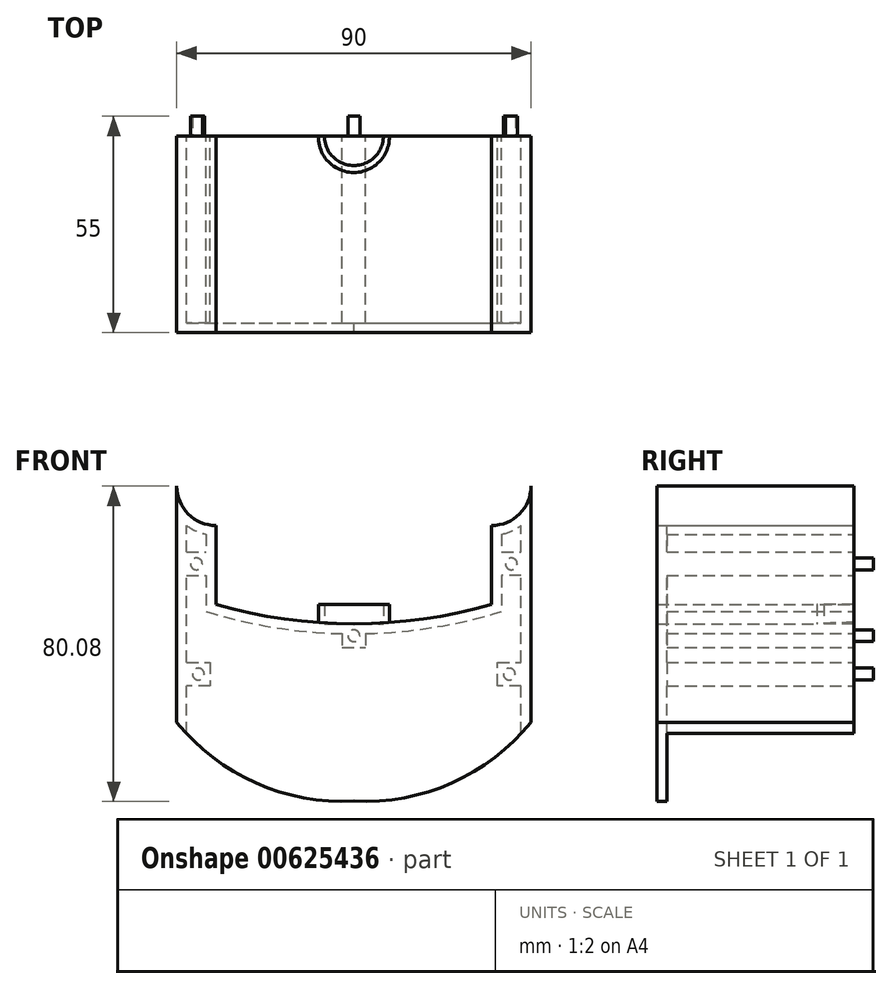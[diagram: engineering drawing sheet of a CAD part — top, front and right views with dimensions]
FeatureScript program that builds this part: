
annotation { "Feature Type Name" : "Feature", "Feature Type Description" : "" }
export const myFeature = defineFeature(function(context is Context, id is Id, definition is map)
    precondition{}
    {
        {
            var Q0;
            Q0=qCreatedBy(makeId("Front.planeOp"),FACE);
            var sketch = newSketch(context, id + "F0", { "sketchPlane" : qUnion([Q0])});
            skLineSegment(sketch, "E0.top", {"start": v(45, -25) * mm, "end": v(-45, -25) * mm});
            skLineSegment(sketch, "E0.left", {"start": v(45, 25) * mm, "end": v(45, -25) * mm});
            skLineSegment(sketch, "E0.right", {"start": v(-45, 25) * mm, "end": v(-45, -25) * mm});
            skPoint(sketch, "E0.middle", {"position": v(0, 0) * mm});
            skLineSegment(sketch, "E1", {"start": v(0, 0) * mm, "end": v(0, -45) * mm});
            skPoint(sketch, "E1.endSnap0", {"position": v(0, -25) * mm});
            skLineSegment(sketch, "E2", {"start": v(-45, 25) * mm, "end": v(-35, 25) * mm});
            skLineSegment(sketch, "E3", {"start": v(45, 25) * mm, "end": v(35, 25) * mm});
            skLineSegment(sketch, "E4", {"start": v(35, 25) * mm, "end": v(35, 5) * mm});
            skLineSegment(sketch, "E5", {"start": v(-35, 25) * mm, "end": v(-35, 5) * mm});
            skArc(sketch, "E6", {"start": v(-35, 5) * mm, "mid": v(0, 0) * mm, "end": v(35, 5) * mm});
            skArc(sketch, "E7", {"start": v(0, -45) * mm, "mid": v(24.91, -40.43) * mm, "end": v(45, -25) * mm});
            skArc(sketch, "E8", {"start": v(-45, -25) * mm, "mid": v(-24.91, -40.43) * mm, "end": v(0, -45) * mm});
            skLineSegment(sketch, "E9", {"start": v(45, 25) * mm, "end": v(45, 35) * mm});
            skLineSegment(sketch, "E10", {"start": v(-45, 25) * mm, "end": v(-45, 35) * mm});
            skArc(sketch, "E11", {"start": v(35, 25) * mm, "mid": v(42.07, 27.93) * mm, "end": v(45, 35) * mm});
            skArc(sketch, "E12", {"start": v(-45, 35) * mm, "mid": v(-42.07, 27.93) * mm, "end": v(-35, 25) * mm});
            skSolve(sketch);
        }
        {
            var Q0;
            Q0=qSketchRegion(id+"F0",true);
            extrude(context, id + "F1", {"entities" : qUnion([Q0]), "depth" : 50 * mm, "offsetDistance" : 25 * mm});
        }
        {
            var Q0;
            Q0=makeQuery(id+"F1.opExtrude","SWEPT_FACE",FACE,{"disambiguationData":[OSD([sQuery(id+"F0.wireOp",EDGE,"E8")])]});
            var Q1;
            Q1=makeQuery(id+"F1.opExtrude","SWEPT_FACE",FACE,{"disambiguationData":[OSD([sQuery(id+"F0.wireOp",EDGE,"E7")])]});
            var Q2;
            Q2=makeQuery(id+"F1.opExtrude","CAP_FACE",FACE,{"disambiguationData":[OSD([sQuery(id+"F0.wireOp",EDGE,"E0.left"),sQuery(id+"F0.wireOp",EDGE,"E0.right"),sQuery(id+"F0.wireOp",EDGE,"E4"),sQuery(id+"F0.wireOp",EDGE,"E5"),sQuery(id+"F0.wireOp",EDGE,"E6"),sQuery(id+"F0.wireOp",EDGE,"E7"),sQuery(id+"F0.wireOp",EDGE,"E8"),sQuery(id+"F0.wireOp",EDGE,"E9"),sQuery(id+"F0.wireOp",EDGE,"E10"),sQuery(id+"F0.wireOp",EDGE,"E11"),sQuery(id+"F0.wireOp",EDGE,"E12")])],"isStart":true});
            shell(context, id + "F2", {"entities" : qUnion([Q0, Q1, Q2]), "thickness" : 2.5 * mm});
        }
        {
            var Q0;
            Q0=qCreatedBy(makeId("Front.planeOp"),FACE);
            var sketch = newSketch(context, id + "F3", { "sketchPlane" : qUnion([Q0])});
            skLineSegment(sketch, "E13", {"start": v(-37.5, 12.25) * mm, "end": v(-42.5, 12.25) * mm});
            skLineSegment(sketch, "E14", {"start": v(-42.5, 12.25) * mm, "end": v(-42.5, 18.25) * mm});
            skLineSegment(sketch, "E15", {"start": v(-42.5, 18.25) * mm, "end": v(-37.5, 18.25) * mm});
            skLineSegment(sketch, "E16", {"start": v(-37.5, 18.25) * mm, "end": v(-37.5, 12.25) * mm});
            skLineSegment(sketch, "E17", {"start": v(37.5, 18.25) * mm, "end": v(37.5, 12.25) * mm});
            skLineSegment(sketch, "E18", {"start": v(37.5, 12.25) * mm, "end": v(42.5, 12.25) * mm});
            skLineSegment(sketch, "E19", {"start": v(42.5, 12.25) * mm, "end": v(42.5, 18.25) * mm});
            skLineSegment(sketch, "E20", {"start": v(42.5, 18.25) * mm, "end": v(37.5, 18.25) * mm});
            skLineSegment(sketch, "E21", {"start": v(0, 0) * mm, "end": v(0, -6) * mm});
            skLineSegment(sketch, "E22", {"start": v(0, -6) * mm, "end": v(-3, -6) * mm});
            skLineSegment(sketch, "E23", {"start": v(-3, -6) * mm, "end": v(3, -6) * mm});
            skLineSegment(sketch, "E24", {"start": v(3, -6) * mm, "end": v(3, 0) * mm});
            skLineSegment(sketch, "E25", {"start": v(-3, -6) * mm, "end": v(-3, 0) * mm});
            skLineSegment(sketch, "E26", {"start": v(-3, 0) * mm, "end": v(3, 0) * mm});
            skLineSegment(sketch, "E27", {"start": v(-42.5, -12.75) * mm, "end": v(-42.5, -9.75) * mm});
            skLineSegment(sketch, "E28", {"start": v(-42.5, -9.75) * mm, "end": v(-42.5, -15.75) * mm});
            skLineSegment(sketch, "E29", {"start": v(-42.5, -15.75) * mm, "end": v(-36.5, -15.75) * mm});
            skLineSegment(sketch, "E30", {"start": v(-36.5, -15.75) * mm, "end": v(-36.5, -9.75) * mm});
            skLineSegment(sketch, "E31", {"start": v(-36.5, -9.75) * mm, "end": v(-42.5, -9.75) * mm});
            skLineSegment(sketch, "E32", {"start": v(42.5, -15.75) * mm, "end": v(42.5, -9.75) * mm});
            skLineSegment(sketch, "E33", {"start": v(42.5, -9.75) * mm, "end": v(36.5, -9.75) * mm});
            skLineSegment(sketch, "E34", {"start": v(36.5, -9.75) * mm, "end": v(36.5, -15.75) * mm});
            skLineSegment(sketch, "E35", {"start": v(36.5, -15.75) * mm, "end": v(42.5, -15.75) * mm});
            skSolve(sketch);
        }
        {
            var Q0;
            Q0 = qSketchRegion(id + "F3", true);
            extrude(context, id + "F4", {"entities" : qUnion([Q0]), "operationType" : NewBodyOperationType.ADD, "depth" : 50 * mm, "offsetDistance" : 25 * mm});
        }
        {
            var Q0;
            {var subQ5=sQuery(id+"F0.wireOp",EDGE,"E0.right");Q0=makeQuery(id+"F0.imprint","IMPRINT",FACE,{"disambiguationData":[TD([[makeQuery(id+"F0.imprint","IMPRINT",EDGE,{"derivedFrom":subQ5}),1.0]])]});}
            var sketch = newSketch(context, id + "F5", { "sketchPlane" : qUnion([Q0])});
            skCircle(sketch, "E36", {"center": v(-40, 15.25) * mm, "radius": 1.5 * mm});
            skCircle(sketch, "E37", {"center": v(-39.5, -12.75) * mm, "radius": 1.5 * mm});
            skCircle(sketch, "E38", {"center": v(40, 15.25) * mm, "radius": 1.5 * mm});
            skCircle(sketch, "E39", {"center": v(39.5, -12.75) * mm, "radius": 1.5 * mm});
            skCircle(sketch, "E40", {"center": v(0, -3) * mm, "radius": 1.5 * mm});
            skSolve(sketch);
        }
        {
            var Q0;
            Q0 = qSketchRegion(id + "F5", true);
            extrude(context, id + "F6", {"entities" : qUnion([Q0]), "operationType" : NewBodyOperationType.ADD, "depth" : -5 * mm, "offsetDistance" : 25 * mm});
        }
        {
            var Q0;
            Q0=qCreatedBy(makeId("Top.planeOp"),FACE);
            var sketch = newSketch(context, id + "F7", { "sketchPlane" : qUnion([Q0])});
            skArc(sketch, "E41", {"start": v(-9, 0) * mm, "mid": v(0, -9.33) * mm, "end": v(9, 0) * mm});
            skLineSegment(sketch, "E42", {"start": v(-9, 0) * mm, "end": v(9, 0) * mm});
            skSolve(sketch);
        }
        {
            var Q0;
            Q0 = qSketchRegion(id + "F7", true);
            extrude(context, id + "F8", {"entities" : qUnion([Q0]), "operationType" : NewBodyOperationType.ADD, "depth" : 5 * mm, "offsetDistance" : 25 * mm});
        }
        {
            var Q0;
            Q0=qCreatedBy(makeId("Top.planeOp"),FACE);
            var sketch = newSketch(context, id + "F9", { "sketchPlane" : qUnion([Q0])});
            skArc(sketch, "E43", {"start": v(-7.5, 0) * mm, "mid": v(0, -7.55) * mm, "end": v(7.5, 0) * mm});
            skLineSegment(sketch, "E44", {"start": v(-7.5, 0) * mm, "end": v(7.5, 0) * mm});
            skSolve(sketch);
        }
        {
            var Q0;
            Q0 = qSketchRegion(id + "F9", true);
            extrude(context, id + "F10", {"entities" : qUnion([Q0]), "operationType" : NewBodyOperationType.REMOVE, "oppositeDirection" : true, "depth" : -6 * mm, "offsetDistance" : 25 * mm});
        }
    });
